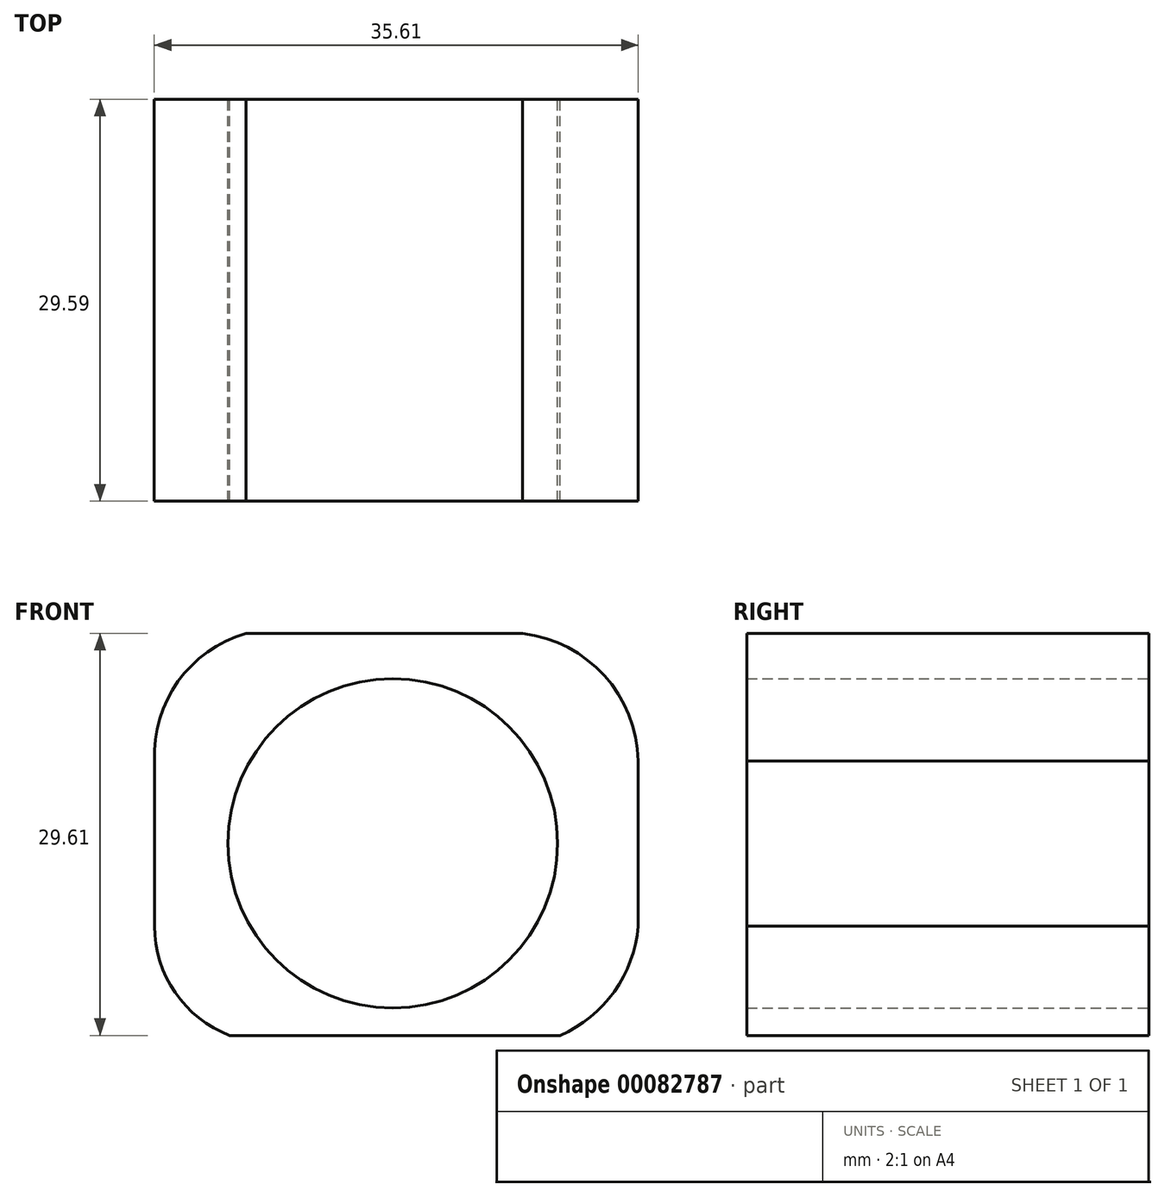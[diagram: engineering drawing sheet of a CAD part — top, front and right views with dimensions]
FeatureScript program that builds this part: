
annotation { "Feature Type Name" : "Feature", "Feature Type Description" : "" }
export const myFeature = defineFeature(function(context is Context, id is Id, definition is map)
    precondition{}
    {
        {
            var Q0;
            Q0=qCreatedBy(makeId("Front.planeOp"),FACE);
            var sketch = newSketch(context, id + "F0", { "sketchPlane" : qUnion([Q0])});
            skLineSegment(sketch, "E0.bottom", {"start": v(0, 0) * mm, "end": v(35.6, 0) * mm});
            skLineSegment(sketch, "E0.top", {"start": v(0, 29.6) * mm, "end": v(35.6, 29.6) * mm});
            skLineSegment(sketch, "E0.left", {"start": v(0, 0) * mm, "end": v(0, 29.6) * mm});
            skLineSegment(sketch, "E0.right", {"start": v(35.6, 0) * mm, "end": v(35.6, 29.6) * mm});
            skArc(sketch, "E1", {"start": v(6.73, 29.6) * mm, "mid": v(1.73, 26.07) * mm, "end": v(0, 20.2) * mm});
            skArc(sketch, "E2", {"start": v(35.6, 20.2) * mm, "mid": v(33.11, 26.5) * mm, "end": v(27.09, 29.6) * mm});
            skArc(sketch, "E3", {"start": v(0, 8.05) * mm, "mid": v(1.52, 3.17) * mm, "end": v(5.54, 0) * mm});
            skArc(sketch, "E4", {"start": v(29.86, 0) * mm, "mid": v(33.84, 3.24) * mm, "end": v(35.6, 8.05) * mm});
            skLineSegment(sketch, "E5", {"start": v(0, 14.8) * mm, "end": v(0, 13.35) * mm});
            skLineSegment(sketch, "E6", {"start": v(35.6, 14.8) * mm, "end": v(35.6, 13.35) * mm});
            skSolve(sketch);
        }
        {
            var Q0;
            Q0=makeQuery(id+"F0.imprint","IMPRINT",FACE,{"disambiguationData":[TD([[makeQuery(id+"F0.imprint","IMPRINT",EDGE,{"derivedFrom":sQuery(id+"F0.wireOp",EDGE,"E0.bottom")}),1.0]])]});
            var sketch = newSketch(context, id + "F1", { "sketchPlane" : qUnion([Q0])});
            skCircle(sketch, "E7", {"center": v(17.54, 14.14) * mm, "radius": 12.13 * mm});
            skSolve(sketch);
        }
        {
            var Q0;
            Q0 = qSketchRegion(id + "F0", true);
            extrude(context, id + "F2", {"entities" : qUnion([Q0]), "depth" : 29.59 * mm});
        }
        {
            var Q0;
            Q0=makeQuery(id+"F1.imprint","IMPRINT",FACE,{"disambiguationData":[TD([[makeQuery(id+"F1.imprint","IMPRINT",EDGE,{"derivedFrom":sQuery(id+"F1.wireOp",EDGE,"E7")}),1.0]])]});
            extrude(context, id + "F3", {"entities" : qUnion([Q0]), "operationType" : NewBodyOperationType.REMOVE, "depth" : 40.3 * mm});
        }
        {
            var Q0;
            {var subQ3=sQuery(id+"F0.wireOp",EDGE,"E2");Q0=makeQuery(id+"F0.imprint","IMPRINT",FACE,{"disambiguationData":[TD([[makeQuery(id+"F0.imprint","IMPRINT",EDGE,{"derivedFrom":subQ3}),-1.0]])]});}
            extrude(context, id + "F4", {"entities" : qUnion([Q0]), "operationType" : NewBodyOperationType.REMOVE, "depth" : 51.04 * mm});
        }
        {
            var Q0;
            {var subQ0=sQuery(id+"F0.wireOp",EDGE,"E0.left");var subQ1=sQuery(id+"F0.wireOp",EDGE,"E0.top");var subQ2=makeQuery(id+"F0.imprint","INTERSECT",VERTEX,{"derivedFrom":[subQ1,subQ0]});Q0=makeQuery(id+"F0.imprint","IMPRINT",FACE,{"disambiguationData":[TD([[makeQuery(id+"F0.imprint","IMPRINT",EDGE,{"disambiguationData":[TD([[subQ2,-1.0]])],"derivedFrom":subQ1}),-1.0]])]});}
            extrude(context, id + "F5", {"entities" : qUnion([Q0]), "operationType" : NewBodyOperationType.REMOVE, "depth" : 43.87 * mm});
        }
        {
            var Q0;
            {var subQ3=sQuery(id+"F0.wireOp",EDGE,"E3");Q0=makeQuery(id+"F0.imprint","IMPRINT",FACE,{"disambiguationData":[TD([[makeQuery(id+"F0.imprint","IMPRINT",EDGE,{"derivedFrom":subQ3}),-1.0]])]});}
            extrude(context, id + "F6", {"entities" : qUnion([Q0]), "operationType" : NewBodyOperationType.REMOVE, "depth" : 37.87 * mm});
        }
        {
            var Q0;
            {var subQ3=sQuery(id+"F0.wireOp",EDGE,"E4");Q0=makeQuery(id+"F0.imprint","IMPRINT",FACE,{"disambiguationData":[TD([[makeQuery(id+"F0.imprint","IMPRINT",EDGE,{"derivedFrom":subQ3}),-1.0]])]});}
            extrude(context, id + "F7", {"entities" : qUnion([Q0]), "operationType" : NewBodyOperationType.REMOVE, "depth" : 46.25 * mm});
        }
    });
